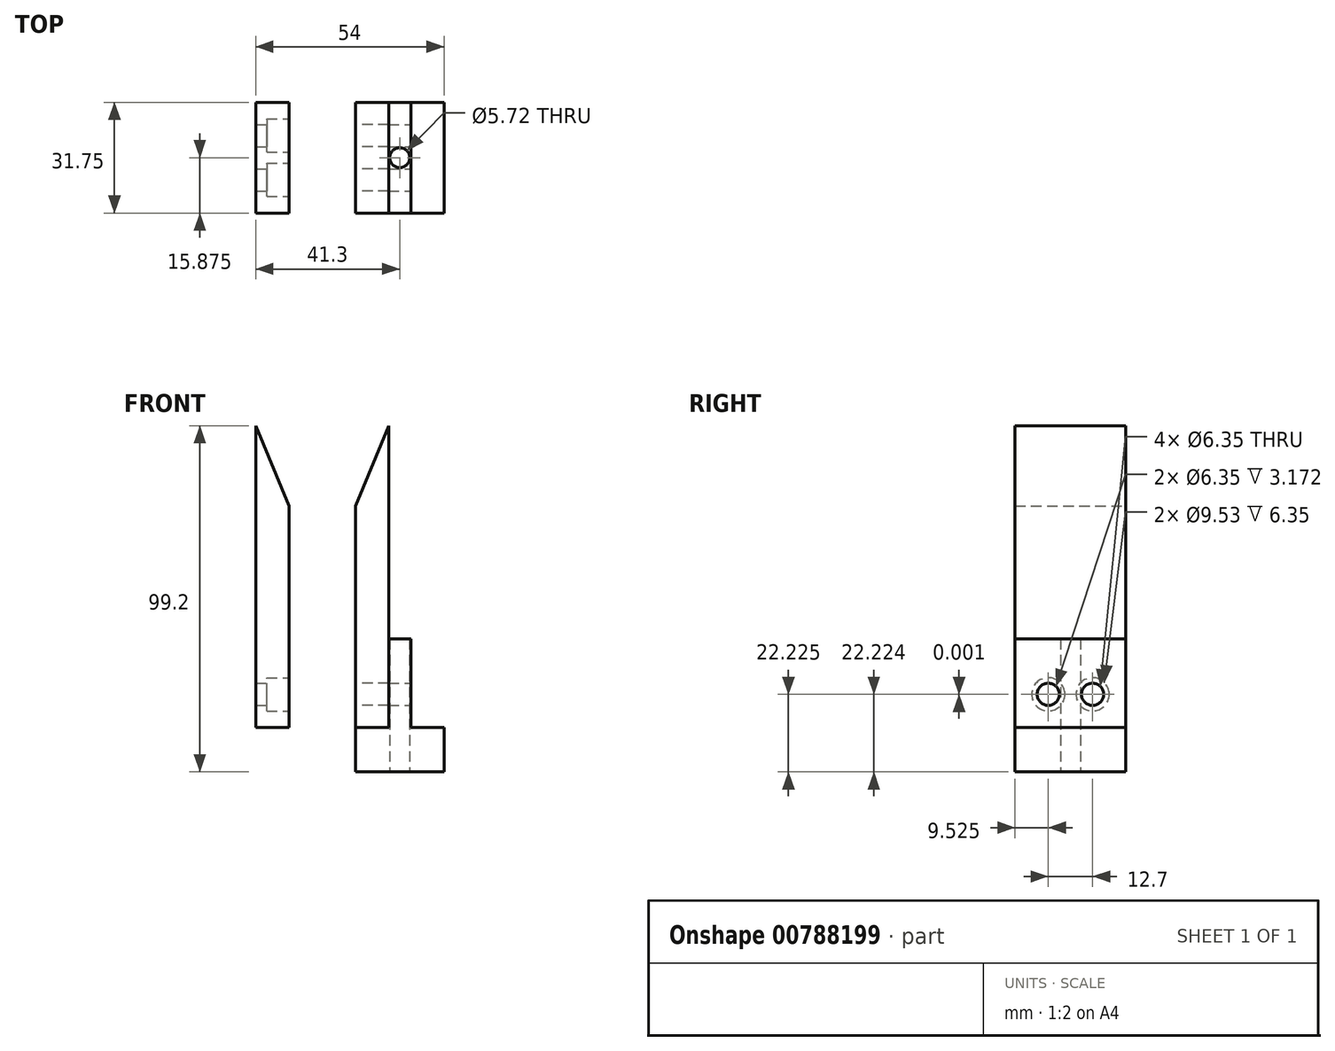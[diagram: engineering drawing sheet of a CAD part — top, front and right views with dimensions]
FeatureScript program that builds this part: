
annotation { "Feature Type Name" : "Feature", "Feature Type Description" : "" }
export const myFeature = defineFeature(function(context is Context, id is Id, definition is map)
    precondition{}
    {
        {
            var Q0;
            Q0=qCreatedBy(makeId("Front.planeOp"),FACE);
            var sketch = newSketch(context, id + "F0", { "sketchPlane" : qUnion([Q0])});
            skLineSegment(sketch, "E0", {"start": v(0, 0) * mm, "end": v(0, 63.5) * mm});
            skLineSegment(sketch, "E1", {"start": v(0, 0) * mm, "end": v(9.52, 0) * mm});
            skLineSegment(sketch, "E2", {"start": v(9.52, 0) * mm, "end": v(9.52, 86.5) * mm});
            skLineSegment(sketch, "E3", {"start": v(0, 63.5) * mm, "end": v(9.52, 86.5) * mm});
            skSolve(sketch);
        }
        {
            var Q0;
            Q0=makeQuery(id+"F0.imprint","IMPRINT",FACE,{"disambiguationData":[TD([[makeQuery(id+"F0.imprint","IMPRINT",EDGE,{"derivedFrom":sQuery(id+"F0.wireOp",EDGE,"E0")}),-1.0]])]});
            extrude(context, id + "F1", {"entities" : qUnion([Q0]), "depth" : 31.75 * mm, "offsetDistance" : 25.4 * mm});
        }
        {
            var Q0;
            Q0=qCreatedBy(makeId("Right.planeOp"),FACE);
            var sketch = newSketch(context, id + "F2", { "sketchPlane" : qUnion([Q0])});
            skCircle(sketch, "E4", {"center": v(-9.53, 9.52) * mm, "radius": 3.18 * mm});
            skCircle(sketch, "E5", {"center": v(-22.23, 9.52) * mm, "radius": 3.18 * mm});
            skSolve(sketch);
        }
        {
            var Q0;
            Q0=qCreatedBy(makeId("Front.planeOp"),FACE);
            var sketch = newSketch(context, id + "F3", { "sketchPlane" : qUnion([Q0])});
            skLineSegment(sketch, "E6", {"start": v(9.53, 0) * mm, "end": v(9.53, 25.4) * mm});
            skLineSegment(sketch, "E7", {"start": v(9.53, 25.4) * mm, "end": v(15.88, 25.4) * mm});
            skLineSegment(sketch, "E8", {"start": v(15.88, 25.4) * mm, "end": v(15.88, 0) * mm});
            skLineSegment(sketch, "E9", {"start": v(15.88, 0) * mm, "end": v(25.4, 0) * mm});
            skLineSegment(sketch, "E10", {"start": v(25.4, 0) * mm, "end": v(25.4, -12.7) * mm});
            skLineSegment(sketch, "E11", {"start": v(25.4, -12.7) * mm, "end": v(0, -12.7) * mm});
            skLineSegment(sketch, "E12", {"start": v(0, -12.7) * mm, "end": v(0, 0) * mm});
            skLineSegment(sketch, "E13", {"start": v(0, 0) * mm, "end": v(9.53, 0) * mm});
            skSolve(sketch);
        }
        {
            var Q0;
            Q0 = qSketchRegion(id + "F3", true);
            extrude(context, id + "F4", {"entities" : qUnion([Q0]), "depth" : 31.75 * mm, "offsetDistance" : 25.4 * mm});
        }
        {
            var Q0;
            Q0 = qSketchRegion(id + "F2", true);
            extrude(context, id + "F5", {"entities" : qUnion([Q0]), "operationType" : NewBodyOperationType.REMOVE, "depth" : 9.52 * mm, "offsetDistance" : 25.4 * mm});
        }
        {
            var Q0;
            Q0=makeQuery(id+"F4.opExtrude","SWEPT_FACE",FACE,{"disambiguationData":[OSD([sQuery(id+"F3.wireOp",EDGE,"E8")])]});
            var sketch = newSketch(context, id + "F6", { "sketchPlane" : qUnion([Q0])});
            skCircle(sketch, "E14", {"center": v(-22.23, 9.52) * mm, "radius": 3.18 * mm});
            skCircle(sketch, "E15", {"center": v(-9.52, 9.52) * mm, "radius": 3.18 * mm});
            skSolve(sketch);
        }
        {
            var Q0;
            Q0 = qSketchRegion(id + "F6", true);
            extrude(context, id + "F7", {"entities" : qUnion([Q0]), "operationType" : NewBodyOperationType.REMOVE, "oppositeDirection" : true, "depth" : 6.35 * mm, "offsetDistance" : 25.4 * mm});
        }
        {
            var Q0;
            Q0=qCreatedBy(makeId("Front.planeOp"),FACE);
            var sketch = newSketch(context, id + "F8", { "sketchPlane" : qUnion([Q0])});
            skLineSegment(sketch, "E16", {"start": v(-19.07, 0) * mm, "end": v(-19.07, 63.5) * mm});
            skLineSegment(sketch, "E17", {"start": v(-28.6, 0) * mm, "end": v(-19.07, 0) * mm});
            skLineSegment(sketch, "E18", {"start": v(-28.6, 86.49) * mm, "end": v(-19.07, 63.5) * mm});
            skLineSegment(sketch, "E19", {"start": v(-28.6, 86.49) * mm, "end": v(-28.6, 0) * mm});
            skSolve(sketch);
        }
        {
            var Q0;
            Q0 = qSketchRegion(id + "F8", true);
            extrude(context, id + "F9", {"entities" : qUnion([Q0]), "depth" : 31.75 * mm, "offsetDistance" : 25.4 * mm});
        }
        {
            var Q0;
            Q0=makeQuery(id+"F9.opExtrude","SWEPT_FACE",FACE,{"disambiguationData":[OSD([sQuery(id+"F8.wireOp",EDGE,"E16")])]});
            var sketch = newSketch(context, id + "F10", { "sketchPlane" : qUnion([Q0])});
            skCircle(sketch, "E20", {"center": v(-9.53, 9.52) * mm, "radius": 3.18 * mm});
            skCircle(sketch, "E21", {"center": v(-22.23, 9.52) * mm, "radius": 3.18 * mm});
            skSolve(sketch);
        }
        {
            var Q0;
            Q0 = qSketchRegion(id + "F10", true);
            extrude(context, id + "F11", {"entities" : qUnion([Q0]), "operationType" : NewBodyOperationType.REMOVE, "oppositeDirection" : true, "depth" : 9.52 * mm, "offsetDistance" : 25.4 * mm});
        }
        {
            var Q0;
            Q0=makeQuery(id+"F9.opExtrude","SWEPT_FACE",FACE,{"disambiguationData":[OSD([sQuery(id+"F8.wireOp",EDGE,"E16")])]});
            var sketch = newSketch(context, id + "F12", { "sketchPlane" : qUnion([Q0])});
            skCircle(sketch, "E22", {"center": v(-22.23, 9.52) * mm, "radius": 4.76 * mm});
            skCircle(sketch, "E23", {"center": v(-9.53, 9.52) * mm, "radius": 4.76 * mm});
            skSolve(sketch);
        }
        {
            var Q0;
            Q0 = qSketchRegion(id + "F12", true);
            extrude(context, id + "F13", {"entities" : qUnion([Q0]), "operationType" : NewBodyOperationType.REMOVE, "oppositeDirection" : true, "depth" : 6.35 * mm, "offsetDistance" : 25.4 * mm});
        }
        {
            var Q0;
            Q0=makeQuery(id+"F4.opExtrude","SWEPT_FACE",FACE,{"disambiguationData":[OSD([sQuery(id+"F3.wireOp",EDGE,"E11")])]});
            var sketch = newSketch(context, id + "F14", { "sketchPlane" : qUnion([Q0])});
            skCircle(sketch, "E24", {"center": v(12.7, 15.88) * mm, "radius": 2.86 * mm});
            skSolve(sketch);
        }
        {
            var Q0;
            Q0 = qSketchRegion(id + "F14", true);
            extrude(context, id + "F15", {"entities" : qUnion([Q0]), "operationType" : NewBodyOperationType.REMOVE, "oppositeDirection" : true, "depth" : 38.1 * mm, "offsetDistance" : 25.4 * mm});
        }
    });
